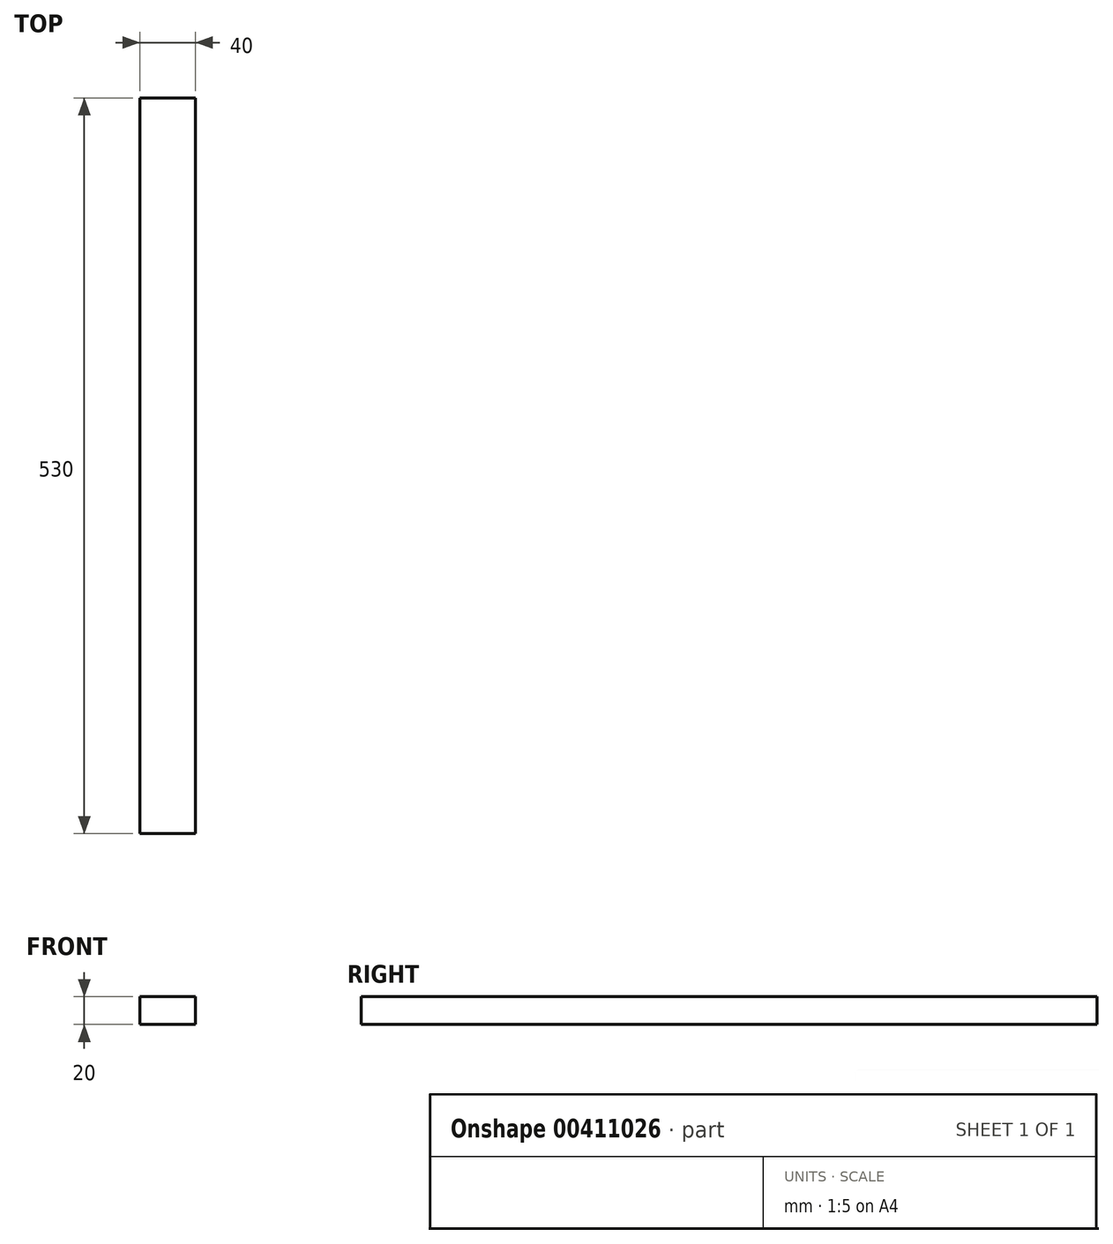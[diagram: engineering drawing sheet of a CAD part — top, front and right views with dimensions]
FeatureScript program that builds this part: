
annotation { "Feature Type Name" : "Feature", "Feature Type Description" : "" }
export const myFeature = defineFeature(function(context is Context, id is Id, definition is map)
    precondition{}
    {
        {
            var Q0;
            Q0=qCreatedBy(makeId("Front.planeOp"),FACE);
            var sketch = newSketch(context, id + "F0", { "sketchPlane" : qUnion([Q0])});
            skLineSegment(sketch, "E0.bottom", {"start": v(20, 10) * mm, "end": v(-20, 10) * mm});
            skLineSegment(sketch, "E0.top", {"start": v(20, -10) * mm, "end": v(-20, -10) * mm});
            skLineSegment(sketch, "E0.left", {"start": v(20, 10) * mm, "end": v(20, -10) * mm});
            skLineSegment(sketch, "E0.right", {"start": v(-20, 10) * mm, "end": v(-20, -10) * mm});
            skPoint(sketch, "E0.middle", {"position": v(0, 0) * mm});
            skSolve(sketch);
        }
        {
            var Q0;
            Q0=makeQuery(id+"F0.imprint","IMPRINT",FACE,{"disambiguationData":[TD([[makeQuery(id+"F0.imprint","IMPRINT",EDGE,{"derivedFrom":sQuery(id+"F0.wireOp",EDGE,"E0.bottom")}),1.0]])]});
            extrude(context, id + "F1", {"entities" : qUnion([Q0]), "depth" : 530 * mm});
        }
    });
